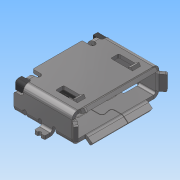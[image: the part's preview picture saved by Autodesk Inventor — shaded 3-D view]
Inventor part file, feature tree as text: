
AUTODESK INVENTOR PART (.ipt)
format: ipt  version: 2016 (Build 200138000, 138)  size: 1,989,632 bytes
history: native  units: mm
features: sketch x2, split x1, extrude x1, imported_body x1
ambient origin geometry x8: Origin, YZ Plane, XZ Plane, XY Plane, X Axis, Y Axis, Z Axis, Center Point
bodies: Body1 (feature_tree)
feature tree (5):
  split  "Split1"
  extrude  "Extrusion4"  [1 undecoded]
  sketch  "Sketch10"  dims[d7=10.0mm d8=0.0mm]
  sketch  "Sketch11"
  imported_body  "Base1"
note: 1 required parameter value undecoded (feature->parameter linkage not recoverable at this tier; creation-order binding heuristic only, values carry confidence <= 0.55)
